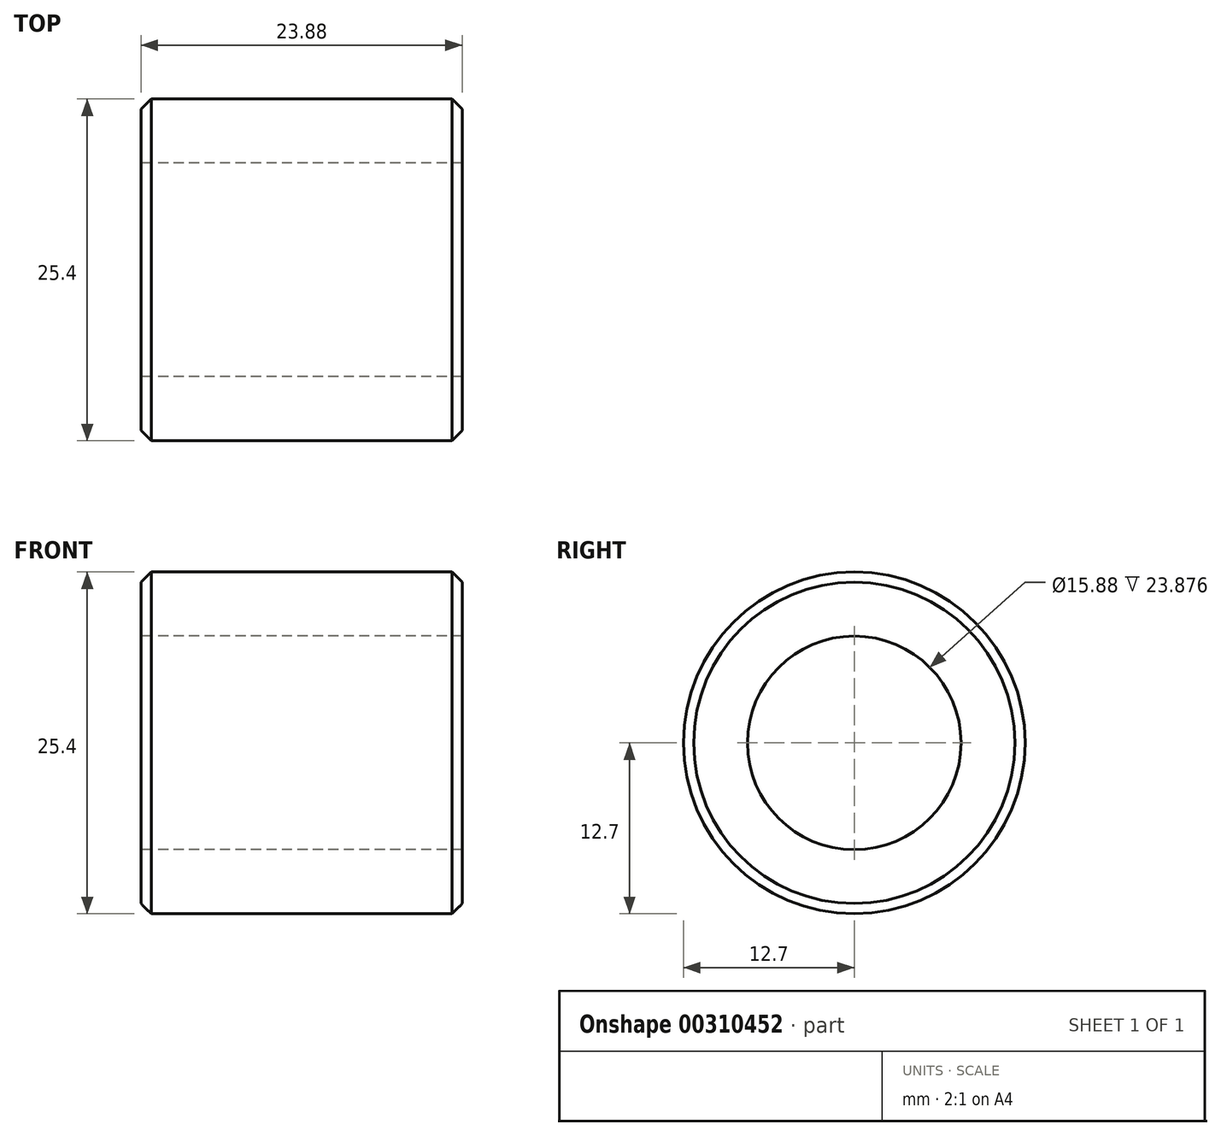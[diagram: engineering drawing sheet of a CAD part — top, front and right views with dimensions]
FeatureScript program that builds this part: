
annotation { "Feature Type Name" : "Feature", "Feature Type Description" : "" }
export const myFeature = defineFeature(function(context is Context, id is Id, definition is map)
    precondition{}
    {
        {
            var Q0;
            Q0=qCreatedBy(makeId("Right.planeOp"),FACE);
            var sketch = newSketch(context, id + "F0", { "sketchPlane" : qUnion([Q0])});
            skCircle(sketch, "E0", {"center": v(0, 0) * mm, "radius": 12.7 * mm});
            skCircle(sketch, "E1", {"center": v(0, 0) * mm, "radius": 7.94 * mm});
            skSolve(sketch);
        }
        {
            var Q0;
            Q0 = qSketchRegion(id + "F0", true);
            extrude(context, id + "F1", {"entities" : qUnion([Q0]), "endBound" : BoundingType.SYMMETRIC, "depth" : 23.88 * mm});
        }
        {
            var Q0;
            Q0=makeQuery(id+"F1.opExtrude","CAP_EDGE",EDGE,{"disambiguationData":[OSD([sQuery(id+"F0.wireOp",EDGE,"E0")])],"isStart":true});
            var Q1;
            Q1=makeQuery(id+"F1.opExtrude","CAP_EDGE",EDGE,{"disambiguationData":[OSD([sQuery(id+"F0.wireOp",EDGE,"E0")])],"isStart":false});
            chamfer(context, id + "F2", {"entities" : qUnion([Q0, Q1]), "width" : 0.76 * mm, "tangentPropagation" : true});
        }
    });
